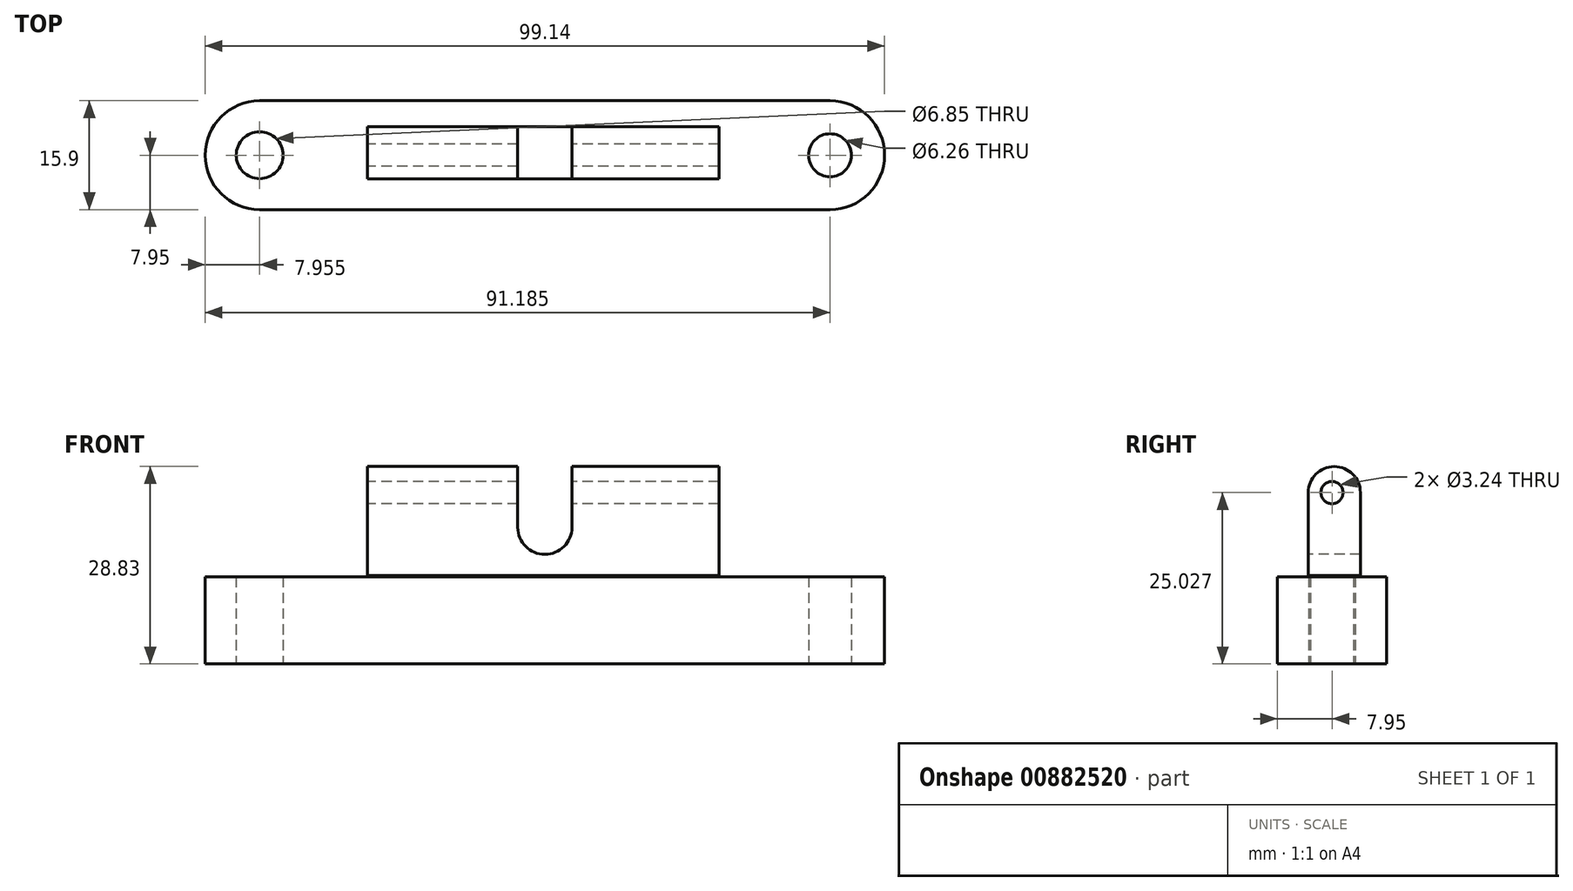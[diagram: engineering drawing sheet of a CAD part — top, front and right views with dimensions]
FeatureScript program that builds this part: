
annotation { "Feature Type Name" : "Feature", "Feature Type Description" : "" }
export const myFeature = defineFeature(function(context is Context, id is Id, definition is map)
    precondition{}
    {
        {
            var Q0;
            Q0=qCreatedBy(makeId("Top.planeOp"),FACE);
            var sketch = newSketch(context, id + "F0", { "sketchPlane" : qUnion([Q0])});
            skLineSegment(sketch, "E0.bottom", {"start": v(41.61, -7.95) * mm, "end": v(-41.61, -7.95) * mm});
            skLineSegment(sketch, "E0.top", {"start": v(41.61, 7.95) * mm, "end": v(-41.61, 7.95) * mm});
            skPoint(sketch, "E0.middle", {"position": v(0, 0) * mm});
            skArc(sketch, "E1", {"start": v(41.61, 7.95) * mm, "mid": v(49.57, 0) * mm, "end": v(41.61, -7.95) * mm});
            skArc(sketch, "E2", {"start": v(-41.61, 7.95) * mm, "mid": v(-49.57, 0) * mm, "end": v(-41.61, -7.95) * mm});
            skCircle(sketch, "E3", {"center": v(-41.61, 0) * mm, "radius": 3.42 * mm});
            skCircle(sketch, "E4", {"center": v(41.61, 0) * mm, "radius": 3.13 * mm});
            skSolve(sketch);
        }
        {
            var Q0;
            Q0=makeQuery(id+"F0.imprint","IMPRINT",FACE,{"disambiguationData":[TD([[makeQuery(id+"F0.imprint","IMPRINT",EDGE,{"derivedFrom":sQuery(id+"F0.wireOp",EDGE,"E0.bottom")}),-1.0]])]});
            extrude(context, id + "F1", {"entities" : qUnion([Q0]), "depth" : 12.7 * mm, "offsetDistance" : 25.4 * mm});
        }
        {
            var Q0;
            Q0=qCreatedBy(makeId("Right.planeOp"),FACE);
            var sketch = newSketch(context, id + "F2", { "sketchPlane" : qUnion([Q0])});
            skLineSegment(sketch, "E5.bottom", {"start": v(-3.46, 12.93) * mm, "end": v(4.15, 12.93) * mm});
            skLineSegment(sketch, "E5.top", {"start": v(-3.46, 25.03) * mm, "end": v(4.15, 25.03) * mm});
            skLineSegment(sketch, "E5.left", {"start": v(-3.46, 12.93) * mm, "end": v(-3.46, 25.03) * mm});
            skLineSegment(sketch, "E5.right", {"start": v(4.15, 12.93) * mm, "end": v(4.15, 25.03) * mm});
            skArc(sketch, "E6", {"start": v(-3.46, 25.03) * mm, "mid": v(0.34, 28.83) * mm, "end": v(4.15, 25.03) * mm});
            skSolve(sketch);
        }
        {
            var Q0;
            Q0=qSketchRegion(id+"F2",true);
            extrude(context, id + "F3", {"entities" : qUnion([Q0]), "depth" : 25.4 * mm, "offsetDistance" : 25.4 * mm});
        }
        {
            var Q0;
            Q0=qSketchRegion(id+"F2",true);
            extrude(context, id + "F4", {"entities" : qUnion([Q0]), "operationType" : NewBodyOperationType.ADD, "oppositeDirection" : true, "depth" : 25.9 * mm, "offsetDistance" : 25.4 * mm});
        }
        {
            var Q0;
            Q0=makeQuery(id+"F4.opExtrude","CAP_FACE",FACE,{"disambiguationData":[OSD([sQuery(id+"F2.wireOp",EDGE,"E5.bottom"),sQuery(id+"F2.wireOp",EDGE,"E5.left"),sQuery(id+"F2.wireOp",EDGE,"E5.right"),sQuery(id+"F2.wireOp",EDGE,"E6")])],"isStart":false});
            var sketch = newSketch(context, id + "F5", { "sketchPlane" : qUnion([Q0])});
            skCircle(sketch, "E7", {"center": v(0, 25.03) * mm, "radius": 1.62 * mm});
            skSolve(sketch);
        }
        {
            var Q0;
            Q0=qSketchRegion(id+"F5",true);
            var Q1;
            Q1=sQuery(id+"F5.wireOp",EDGE,"E7");
            extrude(context, id + "F6", {"entities" : qUnion([Q0]), "operationType" : NewBodyOperationType.REMOVE, "surfaceEntities" : qUnion([Q1]), "oppositeDirection" : true, "depth" : 55.88 * mm, "offsetDistance" : 25.4 * mm});
        }
        {
            var Q0;
            Q0=qCreatedBy(makeId("Front.planeOp"),FACE);
            var sketch = newSketch(context, id + "F7", { "sketchPlane" : qUnion([Q0])});
            skLineSegment(sketch, "E8.bottom", {"start": v(3.95, 19.95) * mm, "end": v(-3.95, 19.95) * mm});
            skLineSegment(sketch, "E8.top", {"start": v(3.95, 42.2) * mm, "end": v(-3.95, 42.2) * mm});
            skLineSegment(sketch, "E8.left", {"start": v(3.95, 19.95) * mm, "end": v(3.95, 42.2) * mm});
            skLineSegment(sketch, "E8.right", {"start": v(-3.95, 19.95) * mm, "end": v(-3.95, 42.2) * mm});
            skPoint(sketch, "E8.middle", {"position": v(0, 31.08) * mm});
            skArc(sketch, "E9", {"start": v(-3.95, 19.95) * mm, "mid": v(0, 16) * mm, "end": v(3.95, 19.95) * mm});
            skSolve(sketch);
        }
        {
            var Q0;
            Q0=qSketchRegion(id+"F7",true);
            extrude(context, id + "F8", {"entities" : qUnion([Q0]), "operationType" : NewBodyOperationType.REMOVE, "oppositeDirection" : true, "depth" : 25.4 * mm, "offsetDistance" : 25.4 * mm});
        }
        {
            var Q0;
            Q0=qSketchRegion(id+"F7",true);
            extrude(context, id + "F9", {"entities" : qUnion([Q0]), "operationType" : NewBodyOperationType.REMOVE, "depth" : 20.83 * mm, "offsetDistance" : 25.4 * mm});
        }
    });
